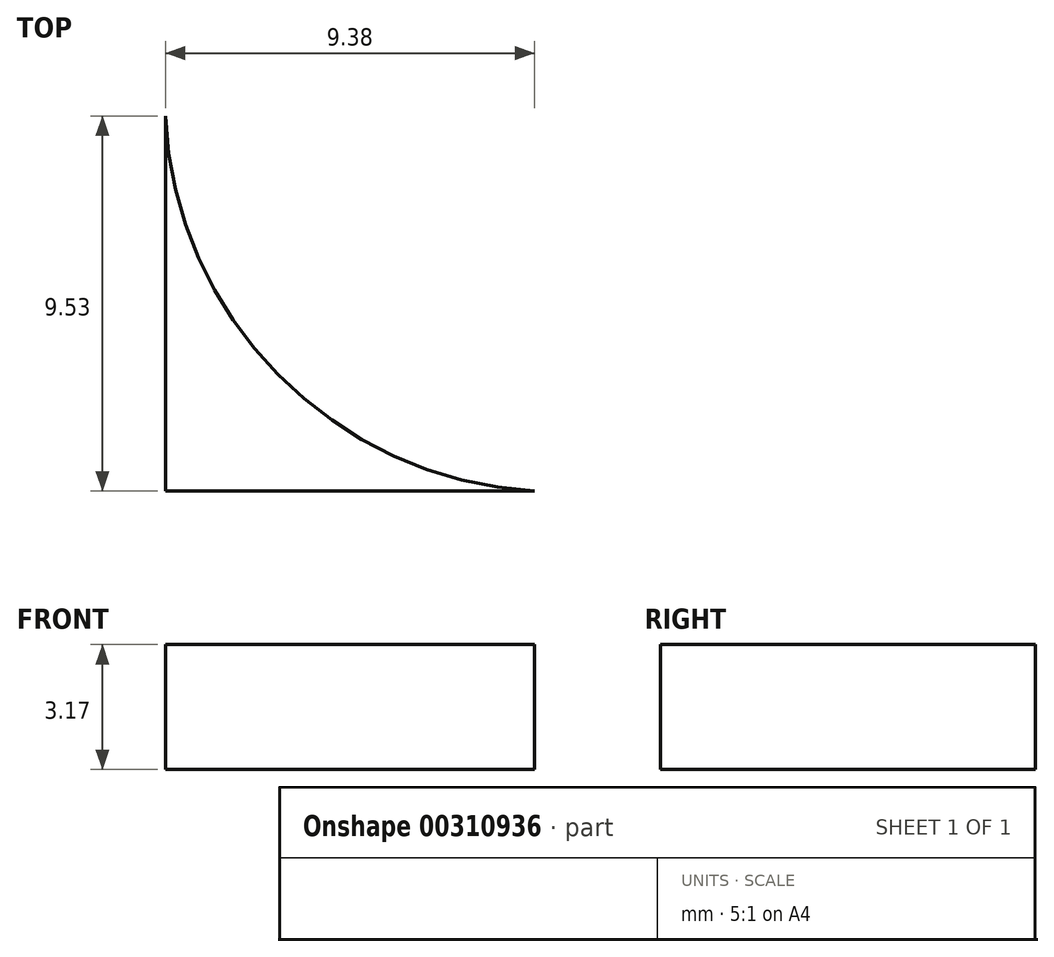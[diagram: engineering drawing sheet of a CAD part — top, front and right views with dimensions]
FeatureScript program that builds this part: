
annotation { "Feature Type Name" : "Feature", "Feature Type Description" : "" }
export const myFeature = defineFeature(function(context is Context, id is Id, definition is map)
    precondition{}
    {
        {
            var Q0;
            Q0=qCreatedBy(makeId("Top.planeOp"),FACE);
            var sketch = newSketch(context, id + "F0", { "sketchPlane" : qUnion([Q0])});
            skLineSegment(sketch, "E0.bottom", {"start": v(0, 0) * mm, "end": v(-38.1, 0) * mm});
            skLineSegment(sketch, "E0.top", {"start": v(0, 19.05) * mm, "end": v(-38.1, 19.05) * mm});
            skLineSegment(sketch, "E0.left", {"start": v(0, 0) * mm, "end": v(0, 19.05) * mm});
            skLineSegment(sketch, "E0.right", {"start": v(-38.1, 0) * mm, "end": v(-38.1, 19.05) * mm});
            skSolve(sketch);
        }
        {
            var Q0;
            Q0=makeQuery(id+"F0.imprint","IMPRINT",FACE,{"disambiguationData":[TD([[makeQuery(id+"F0.imprint","IMPRINT",EDGE,{"derivedFrom":sQuery(id+"F0.wireOp",EDGE,"E0.bottom")}),-1.0]])]});
            extrude(context, id + "F1", {"entities" : qUnion([Q0]), "depth" : 3.17 * mm});
        }
        {
            var Q0;
            Q0=makeQuery(id+"F1.opExtrude","CAP_FACE",FACE,{"disambiguationData":[OSD([sQuery(id+"F0.wireOp",EDGE,"E0.bottom"),sQuery(id+"F0.wireOp",EDGE,"E0.top"),sQuery(id+"F0.wireOp",EDGE,"E0.left"),sQuery(id+"F0.wireOp",EDGE,"E0.right")])],"isStart":false});
            var sketch = newSketch(context, id + "F2", { "sketchPlane" : qUnion([Q0])});
            skLineSegment(sketch, "E1", {"start": v(-38.1, 9.52) * mm, "end": v(0, 9.53) * mm, "construction": true});
            skArc(sketch, "E2", {"start": v(-28.72, 19.05) * mm, "mid": v(-35.24, 16.09) * mm, "end": v(-38.1, 9.52) * mm});
            skArc(sketch, "E3.MirrorCS", {"start": v(-28.72, 0) * mm, "mid": v(-35.24, 2.96) * mm, "end": v(-38.1, 9.53) * mm});
            skCircle(sketch, "E4", {"center": v(-33.7, 9.52) * mm, "radius": 2.48 * mm});
            skSolve(sketch);
        }
        {
            var Q0;
            {var subQ0=sQuery(id+"F2.wireOp",EDGE,"E2");Q0=makeQuery(id+"F2.imprint","IMPRINT",FACE,{"disambiguationData":[TD([[makeQuery(id+"F2.imprint","IMPRINT",EDGE,{"derivedFrom":subQ0}),-1.0]])]});}
            var Q1;
            {var subQ0=sQuery(id+"F2.wireOp",EDGE,"E3.MirrorCS");Q1=makeQuery(id+"F2.imprint","IMPRINT",FACE,{"disambiguationData":[TD([[makeQuery(id+"F2.imprint","IMPRINT",EDGE,{"derivedFrom":subQ0}),1.0]])]});}
            var Q2;
            Q2=makeQuery(id+"F2.imprint","IMPRINT",FACE,{"disambiguationData":[TD([[makeQuery(id+"F2.imprint","IMPRINT",EDGE,{"derivedFrom":sQuery(id+"F2.wireOp",EDGE,"E4")}),1.0]])]});
            extrude(context, id + "F3", {"entities" : qUnion([Q0, Q1, Q2]), "operationType" : NewBodyOperationType.REMOVE, "endBound" : BoundingType.THROUGH_ALL, "oppositeDirection" : true, "depth" : 25.4 * mm});
        }
        {
            var Q0;
            Q0=makeQuery(id+"F1.opExtrude","CAP_FACE",FACE,{"disambiguationData":[OSD([sQuery(id+"F0.wireOp",EDGE,"E0.bottom"),sQuery(id+"F0.wireOp",EDGE,"E0.top"),sQuery(id+"F0.wireOp",EDGE,"E0.left"),sQuery(id+"F0.wireOp",EDGE,"E0.right")])],"isStart":false});
            var sketch = newSketch(context, id + "F4", { "sketchPlane" : qUnion([Q0])});
            skLineSegment(sketch, "E5", {"start": v(-16.26, 9.77) * mm, "end": v(-11.2, 9.77) * mm});
            skLineSegment(sketch, "E6", {"start": v(-11.23, 11.53) * mm, "end": v(-16.4, 11.53) * mm});
            skCircle(sketch, "E7", {"center": v(-20.36, 10.7) * mm, "radius": 3.04 * mm});
            skArc(sketch, "E8", {"start": v(-16.64, 11.53) * mm, "mid": v(-24.18, 10.74) * mm, "end": v(-16.66, 9.77) * mm});
            skCircle(sketch, "E9", {"center": v(-7.4, 10.7) * mm, "radius": 3.4 * mm});
            skArc(sketch, "E10", {"start": v(-11.2, 9.77) * mm, "mid": v(-3.47, 10.74) * mm, "end": v(-11.23, 11.53) * mm});
            skLineSegment(sketch, "E11", {"start": v(-7.7, 12.57) * mm, "end": v(-7.63, 12.55) * mm});
            skLineSegment(sketch, "E12", {"start": v(-6.99, 12.57) * mm, "end": v(-6.99, 12.52) * mm});
            skLineSegment(sketch, "E13", {"start": v(-6.05, 10.2) * mm, "end": v(-6, 10.16) * mm});
            skLineSegment(sketch, "E14", {"start": v(-16.26, 9.77) * mm, "end": v(-16.66, 9.77) * mm});
            skLineSegment(sketch, "E15", {"start": v(-16.4, 11.53) * mm, "end": v(-16.66, 11.53) * mm});
            skLineSegment(sketch, "E16", {"start": v(-22.34, 11.41) * mm, "end": v(-22.34, 10.06) * mm});
            skLineSegment(sketch, "E17", {"start": v(-22.34, 10.06) * mm, "end": v(-22.17, 10.06) * mm});
            skLineSegment(sketch, "E18", {"start": v(-22.17, 10.06) * mm, "end": v(-22.17, 11.41) * mm});
            skLineSegment(sketch, "E19", {"start": v(-22.17, 11.41) * mm, "end": v(-21.75, 11.41) * mm});
            skLineSegment(sketch, "E20", {"start": v(-21.75, 11.41) * mm, "end": v(-21.75, 11.6) * mm});
            skLineSegment(sketch, "E21", {"start": v(-21.75, 11.6) * mm, "end": v(-22.92, 11.6) * mm});
            skLineSegment(sketch, "E22", {"start": v(-22.92, 11.6) * mm, "end": v(-22.92, 11.41) * mm});
            skLineSegment(sketch, "E23", {"start": v(-22.92, 11.41) * mm, "end": v(-22.34, 11.41) * mm});
            skPoint(sketch, "E24", {"position": v(-22.34, 11.6) * mm});
            skPoint(sketch, "E25.start.orphan", {"position": v(-19.8, 11.44) * mm});
            skPoint(sketch, "E26.end.orphan", {"position": v(-18.8, 11.44) * mm});
            skFitSpline(sketch, "E27", {"points": [v(-20.19, 11.15) * mm, v(-20.38, 11.49) * mm, v(-20.65, 11.59) * mm, v(-21.02, 11.58) * mm, v(-21.31, 11.41) * mm, v(-21.57, 10.87) * mm, v(-21.39, 10.3) * mm, v(-21.02, 10) * mm, v(-20.54, 10.04) * mm, v(-20.29, 10.26) * mm, v(-20.19, 10.49) * mm, v(-20.38, 10.54) * mm, v(-20.52, 10.26) * mm, v(-20.97, 10.22) * mm, v(-21.29, 10.49) * mm, v(-21.32, 10.89) * mm, v(-21.2, 11.24) * mm, v(-20.8, 11.45) * mm, v(-20.48, 11.28) * mm, v(-20.43, 11.14) * mm, v(-20.19, 11.15) * mm]});
            skLineSegment(sketch, "E28", {"start": v(-19.93, 10.06) * mm, "end": v(-19.93, 11.58) * mm});
            skLineSegment(sketch, "E29", {"start": v(-19.93, 11.58) * mm, "end": v(-19.71, 11.58) * mm});
            skLineSegment(sketch, "E30", {"start": v(-19.71, 11.58) * mm, "end": v(-18.9, 10.4) * mm});
            skLineSegment(sketch, "E31", {"start": v(-18.9, 10.4) * mm, "end": v(-18.9, 11.58) * mm});
            skLineSegment(sketch, "E32", {"start": v(-18.9, 11.58) * mm, "end": v(-18.69, 11.58) * mm});
            skLineSegment(sketch, "E33", {"start": v(-18.69, 11.58) * mm, "end": v(-18.69, 10.04) * mm});
            skLineSegment(sketch, "E34", {"start": v(-18.69, 10.04) * mm, "end": v(-18.98, 10.04) * mm});
            skLineSegment(sketch, "E35", {"start": v(-18.98, 10.04) * mm, "end": v(-19.7, 11.17) * mm});
            skLineSegment(sketch, "E36", {"start": v(-19.7, 11.17) * mm, "end": v(-19.7, 10.04) * mm});
            skLineSegment(sketch, "E37", {"start": v(-19.7, 10.04) * mm, "end": v(-19.93, 10.06) * mm});
            skLineSegment(sketch, "E38", {"start": v(-17.59, 11.49) * mm, "end": v(-17.59, 10.37) * mm});
            skLineSegment(sketch, "E39", {"start": v(-17.59, 11.49) * mm, "end": v(-17.59, 11.59) * mm});
            skLineSegment(sketch, "E40", {"start": v(-17.59, 11.59) * mm, "end": v(-17.8, 11.59) * mm});
            skLineSegment(sketch, "E41", {"start": v(-17.8, 11.59) * mm, "end": v(-17.8, 10.37) * mm});
            skFitSpline(sketch, "E42", {"points": [v(-17.8, 10.37) * mm, v(-17.93, 10.2) * mm, v(-18.24, 10.26) * mm, v(-18.27, 10.48) * mm, v(-18.47, 10.49) * mm, v(-18.38, 10.13) * mm, v(-18.02, 10) * mm, v(-17.72, 10.1) * mm, v(-17.59, 10.37) * mm], "startDerivative": vector(-0.68, -2.04) * mm, "endDerivative": vector(0.7, 2.36) * mm});
            skPoint(sketch, "E43.end.orphan", {"position": v(-6.67, 12.57) * mm});
            skPoint(sketch, "E44.start.orphan", {"position": v(-6.22, 12.57) * mm});
            skPoint(sketch, "E45.start.orphan", {"position": v(-5.33, 12.57) * mm});
            skFitSpline(sketch, "E46", {"points": [v(-8.57, 12.27) * mm, v(-8.7, 12.54) * mm, v(-9.17, 12.6) * mm, v(-9.43, 12.4) * mm, v(-9.4, 12.12) * mm, v(-9.13, 11.99) * mm, v(-8.82, 11.9) * mm, v(-8.7, 11.8) * mm, v(-8.79, 11.6) * mm, v(-9.1, 11.58) * mm, v(-9.3, 11.7) * mm, v(-9.35, 11.87) * mm, v(-9.5, 11.85) * mm, v(-9.35, 11.52) * mm, v(-8.98, 11.42) * mm, v(-8.62, 11.53) * mm, v(-8.57, 11.82) * mm, v(-8.72, 12.05) * mm, v(-9.05, 12.11) * mm, v(-9.25, 12.25) * mm, v(-9.26, 12.41) * mm, v(-8.9, 12.46) * mm, v(-8.71, 12.29) * mm, v(-8.57, 12.27) * mm]});
            skLineSegment(sketch, "E47", {"start": v(-8.42, 12.59) * mm, "end": v(-8.17, 11.46) * mm});
            skLineSegment(sketch, "E48", {"start": v(-8.17, 11.46) * mm, "end": v(-7.98, 11.46) * mm});
            skLineSegment(sketch, "E49", {"start": v(-7.98, 11.46) * mm, "end": v(-7.7, 12.47) * mm});
            skLineSegment(sketch, "E50", {"start": v(-7.7, 12.47) * mm, "end": v(-7.63, 12.45) * mm});
            skLineSegment(sketch, "E51", {"start": v(-7.63, 12.45) * mm, "end": v(-7.36, 11.37) * mm});
            skLineSegment(sketch, "E52", {"start": v(-7.36, 11.37) * mm, "end": v(-7.23, 11.4) * mm});
            skLineSegment(sketch, "E53", {"start": v(-7.23, 11.4) * mm, "end": v(-6.99, 12.57) * mm});
            skLineSegment(sketch, "E54", {"start": v(-6.99, 12.57) * mm, "end": v(-7.1, 12.6) * mm});
            skLineSegment(sketch, "E55", {"start": v(-7.1, 12.6) * mm, "end": v(-7.3, 11.6) * mm});
            skLineSegment(sketch, "E56", {"start": v(-7.3, 11.6) * mm, "end": v(-7.63, 12.55) * mm});
            skLineSegment(sketch, "E57", {"start": v(-7.7, 12.57) * mm, "end": v(-7.8, 12.6) * mm});
            skLineSegment(sketch, "E58", {"start": v(-7.8, 12.6) * mm, "end": v(-8.1, 11.61) * mm});
            skLineSegment(sketch, "E59", {"start": v(-8.1, 11.61) * mm, "end": v(-8.27, 12.52) * mm});
            skLineSegment(sketch, "E60", {"start": v(-8.27, 12.52) * mm, "end": v(-8.27, 12.59) * mm});
            skLineSegment(sketch, "E61", {"start": v(-8.27, 12.59) * mm, "end": v(-8.42, 12.59) * mm});
            skLineSegment(sketch, "E62", {"start": v(-6.57, 11.46) * mm, "end": v(-6.57, 12.57) * mm});
            skLineSegment(sketch, "E63", {"start": v(-6.57, 12.57) * mm, "end": v(-6.67, 12.57) * mm});
            skLineSegment(sketch, "E64", {"start": v(-6.57, 11.46) * mm, "end": v(-6.76, 11.46) * mm});
            skLineSegment(sketch, "E65", {"start": v(-6.76, 11.46) * mm, "end": v(-6.76, 12.59) * mm});
            skLineSegment(sketch, "E66", {"start": v(-6.76, 12.59) * mm, "end": v(-6.57, 12.57) * mm});
            skLineSegment(sketch, "E67", {"start": v(-6.3, 11.46) * mm, "end": v(-6.3, 12.57) * mm});
            skLineSegment(sketch, "E68", {"start": v(-6.3, 12.57) * mm, "end": v(-6.09, 12.57) * mm});
            skLineSegment(sketch, "E69", {"start": v(-6.09, 12.57) * mm, "end": v(-5.73, 11.6) * mm});
            skLineSegment(sketch, "E70", {"start": v(-5.73, 11.6) * mm, "end": v(-5.33, 12.57) * mm});
            skLineSegment(sketch, "E71", {"start": v(-5.33, 12.57) * mm, "end": v(-5.19, 12.59) * mm});
            skLineSegment(sketch, "E72", {"start": v(-5.19, 12.59) * mm, "end": v(-5.19, 11.46) * mm});
            skLineSegment(sketch, "E73", {"start": v(-5.19, 11.46) * mm, "end": v(-5.33, 11.49) * mm});
            skLineSegment(sketch, "E74", {"start": v(-5.33, 11.49) * mm, "end": v(-5.33, 12.47) * mm});
            skLineSegment(sketch, "E75", {"start": v(-5.33, 12.47) * mm, "end": v(-5.7, 11.46) * mm});
            skLineSegment(sketch, "E76", {"start": v(-5.7, 11.46) * mm, "end": v(-5.8, 11.48) * mm});
            skLineSegment(sketch, "E77", {"start": v(-5.8, 11.48) * mm, "end": v(-6.15, 12.47) * mm});
            skLineSegment(sketch, "E78", {"start": v(-6.15, 12.47) * mm, "end": v(-6.15, 11.46) * mm});
            skLineSegment(sketch, "E79", {"start": v(-6.15, 11.46) * mm, "end": v(-6.3, 11.46) * mm});
            skFitSpline(sketch, "E80", {"points": [v(-8.46, 10.45) * mm, v(-8.6, 10.67) * mm, v(-8.92, 10.78) * mm, v(-9.3, 10.67) * mm, v(-9.48, 10.12) * mm, v(-9.23, 9.63) * mm, v(-8.8, 9.6) * mm, v(-8.48, 9.79) * mm, v(-8.45, 9.97) * mm, v(-8.58, 10.01) * mm, v(-8.7, 9.8) * mm, v(-9.01, 9.75) * mm, v(-9.3, 10) * mm, v(-9.3, 10.46) * mm, v(-8.92, 10.65) * mm, v(-8.67, 10.56) * mm, v(-8.58, 10.4) * mm, v(-8.46, 10.45) * mm]});
            skLineSegment(sketch, "E81", {"start": v(-8.23, 10.74) * mm, "end": v(-8.23, 9.63) * mm});
            skLineSegment(sketch, "E82", {"start": v(-8.23, 9.63) * mm, "end": v(-7.52, 9.63) * mm});
            skLineSegment(sketch, "E83", {"start": v(-7.52, 9.63) * mm, "end": v(-7.52, 9.71) * mm});
            skLineSegment(sketch, "E84", {"start": v(-7.52, 9.71) * mm, "end": v(-8.1, 9.71) * mm});
            skLineSegment(sketch, "E85", {"start": v(-8.1, 9.71) * mm, "end": v(-8.1, 10.77) * mm});
            skLineSegment(sketch, "E86", {"start": v(-8.1, 10.77) * mm, "end": v(-8.23, 10.74) * mm});
            skPoint(sketch, "E87.0.internal.orphan", {"position": v(-7.17, 10.7) * mm});
            skPoint(sketch, "E87.11.internal.orphan", {"position": v(-7.29, 10.7) * mm});
            skPoint(sketch, "E88.0.internal.orphan", {"position": v(-5.58, 10.72) * mm});
            skPoint(sketch, "E88.3.internal.orphan", {"position": v(-5.58, 10.2) * mm});
            skPoint(sketch, "E88.6.internal.orphan", {"position": v(-5.58, 9.66) * mm});
            skLineSegment(sketch, "E89", {"start": v(-6.38, 10.7) * mm, "end": v(-6.38, 9.93) * mm});
            skFitSpline(sketch, "E90", {"points": [v(-6.38, 9.93) * mm, v(-6.55, 9.63) * mm, v(-7.08, 9.64) * mm, v(-7.3, 9.93) * mm], "startDerivative": vector(-0.31, -1.17) * mm, "endDerivative": vector(-0.49, 1.07) * mm});
            skLineSegment(sketch, "E91", {"start": v(-7.3, 9.93) * mm, "end": v(-7.29, 10.8) * mm});
            skLineSegment(sketch, "E92", {"start": v(-7.29, 10.8) * mm, "end": v(-7.17, 10.8) * mm});
            skLineSegment(sketch, "E93", {"start": v(-7.17, 10.8) * mm, "end": v(-7.17, 9.93) * mm});
            skLineSegment(sketch, "E94", {"start": v(-7.17, 9.93) * mm, "end": v(-7.14, 9.98) * mm});
            skFitSpline(sketch, "E95", {"points": [v(-7.17, 9.93) * mm, v(-7, 9.72) * mm, v(-6.66, 9.73) * mm, v(-6.55, 9.93) * mm], "startDerivative": vector(0.38, -0.74) * mm, "endDerivative": vector(0.2, 0.75) * mm});
            skLineSegment(sketch, "E96", {"start": v(-6.55, 9.93) * mm, "end": v(-6.55, 10.77) * mm});
            skLineSegment(sketch, "E97", {"start": v(-6.55, 10.77) * mm, "end": v(-6.38, 10.77) * mm});
            skLineSegment(sketch, "E98", {"start": v(-6.38, 10.77) * mm, "end": v(-6.38, 10.7) * mm});
            skLineSegment(sketch, "E99", {"start": v(-6.12, 10.7) * mm, "end": v(-6.12, 9.62) * mm});
            skLineSegment(sketch, "E100", {"start": v(-6.12, 9.62) * mm, "end": v(-5.5, 9.62) * mm});
            skLineSegment(sketch, "E101", {"start": v(-5.5, 9.62) * mm, "end": v(-5.5, 9.55) * mm});
            skLineSegment(sketch, "E102", {"start": v(-6.12, 10.7) * mm, "end": v(-6.12, 10.82) * mm});
            skLineSegment(sketch, "E103", {"start": v(-6.12, 10.82) * mm, "end": v(-5.58, 10.82) * mm});
            skFitSpline(sketch, "E104", {"points": [v(-5.58, 10.82) * mm, v(-5.32, 10.6) * mm, v(-5.41, 10.26) * mm, v(-5.48, 10.22) * mm, v(-5.26, 10.1) * mm, v(-5.32, 9.66) * mm, v(-5.5, 9.62) * mm], "startDerivative": vector(1.8, -0.84) * mm, "endDerivative": vector(-1.36, 0.16) * mm});
            skLineSegment(sketch, "E105", {"start": v(-5.97, 10.66) * mm, "end": v(-5.97, 10.27) * mm});
            skLineSegment(sketch, "E106", {"start": v(-5.97, 10.27) * mm, "end": v(-5.58, 10.27) * mm});
            skLineSegment(sketch, "E107", {"start": v(-5.97, 10.66) * mm, "end": v(-5.48, 10.66) * mm});
            skFitSpline(sketch, "E108", {"points": [v(-5.48, 10.66) * mm, v(-5.46, 10.5) * mm, v(-5.58, 10.27) * mm], "startDerivative": vector(0.09, -0.35) * mm, "endDerivative": vector(-0.27, -0.42) * mm});
            skLineSegment(sketch, "E109", {"start": v(-5.96, 9.73) * mm, "end": v(-6, 10.16) * mm});
            skLineSegment(sketch, "E110", {"start": v(-6, 10.16) * mm, "end": v(-5.58, 10.16) * mm});
            skFitSpline(sketch, "E111", {"points": [v(-5.58, 10.16) * mm, v(-5.38, 10.06) * mm, v(-5.42, 9.78) * mm, v(-5.58, 9.66) * mm], "startDerivative": vector(0.76, -0.18) * mm, "endDerivative": vector(-0.55, -0.27) * mm});
            skLineSegment(sketch, "E112", {"start": v(-5.96, 9.73) * mm, "end": v(-5.52, 9.69) * mm});
            skSolve(sketch);
        }
        {
            var Q0;
            Q0=makeQuery(id+"F4.imprint","IMPRINT",FACE,{"disambiguationData":[TD([[makeQuery(id+"F4.imprint","IMPRINT",EDGE,{"derivedFrom":sQuery(id+"F4.wireOp",EDGE,"E105")}),1.0]])]});
            var Q1;
            {var subQ0=sQuery(id+"F4.wireOp",EDGE,"E109");Q1=makeQuery(id+"F4.imprint","IMPRINT",FACE,{"disambiguationData":[TD([[makeQuery(id+"F4.imprint","IMPRINT",EDGE,{"derivedFrom":subQ0}),-1.0]])]});}
            var Q2;
            Q2=makeQuery(id+"F4.imprint","IMPRINT",FACE,{"disambiguationData":[TD([[makeQuery(id+"F4.imprint","IMPRINT",EDGE,{"derivedFrom":sQuery(id+"F4.wireOp",EDGE,"E7")}),1.0]])]});
            var Q3;
            Q3=makeQuery(id+"F4.imprint","IMPRINT",FACE,{"disambiguationData":[TD([[makeQuery(id+"F4.imprint","IMPRINT",EDGE,{"derivedFrom":sQuery(id+"F4.wireOp",EDGE,"E9")}),1.0]])]});
            var Q4;
            Q4=makeQuery(id+"F4.imprint","IMPRINT",FACE,{"disambiguationData":[TD([[makeQuery(id+"F4.imprint","IMPRINT",EDGE,{"derivedFrom":sQuery(id+"F4.wireOp",EDGE,"E5")}),-1.0]])]});
            extrude(context, id + "F5", {"entities" : qUnion([Q0, Q1, Q2, Q3, Q4]), "operationType" : NewBodyOperationType.REMOVE, "oppositeDirection" : true, "depth" : 0.25 * mm});
        }
    });
